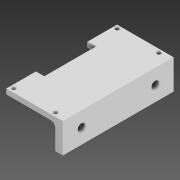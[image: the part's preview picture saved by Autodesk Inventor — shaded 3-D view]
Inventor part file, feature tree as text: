
AUTODESK INVENTOR PART (.ipt)
format: ipt  version: 2020 (Build 240168000, 168)  size: 133,120 bytes
history: native  units: in
note: dims shown in document units (in); Inventor stores cm internally (conversion verified against a paired STEP export)
features: extrude x3, sketch x3, fillet x1
ambient origin geometry x8: Origin, YZ Plane, XZ Plane, XY Plane, X Axis, Y Axis, Z Axis, Center Point
bodies: Solid1 (feature_tree)
feature tree (7):
  extrude  "Extrusion1"  Depth=1.7717in
  extrude  "Extrusion2"  Depth=0.0591in
  fillet  "Fillet1"  Radius=0.0591in
  extrude  "Extrusion3"  Depth=0.0591in
  sketch  "Sketch1"  dims[d0=0.7874in d1=1.7717in]
  sketch  "Sketch2"  dims[d2=0.6693in d3=1.6535in d4=0.0591in]
  sketch  "Sketch3"  dims[d5=0.0591in d6=0.0591in d7=0.0591in d8=0.0787in d9=0.0in d10=0.1181in d11=1.7717in d12=0.3937in d13=0.0787in d14=0.0in d15=0.0in d16=0.0787in d17=0.1969in d18=0.0394in d19=0.5906in d20=1.1811in d21=0.1181in d22=0.1181in d23=0.3937in d24=0.0in]
